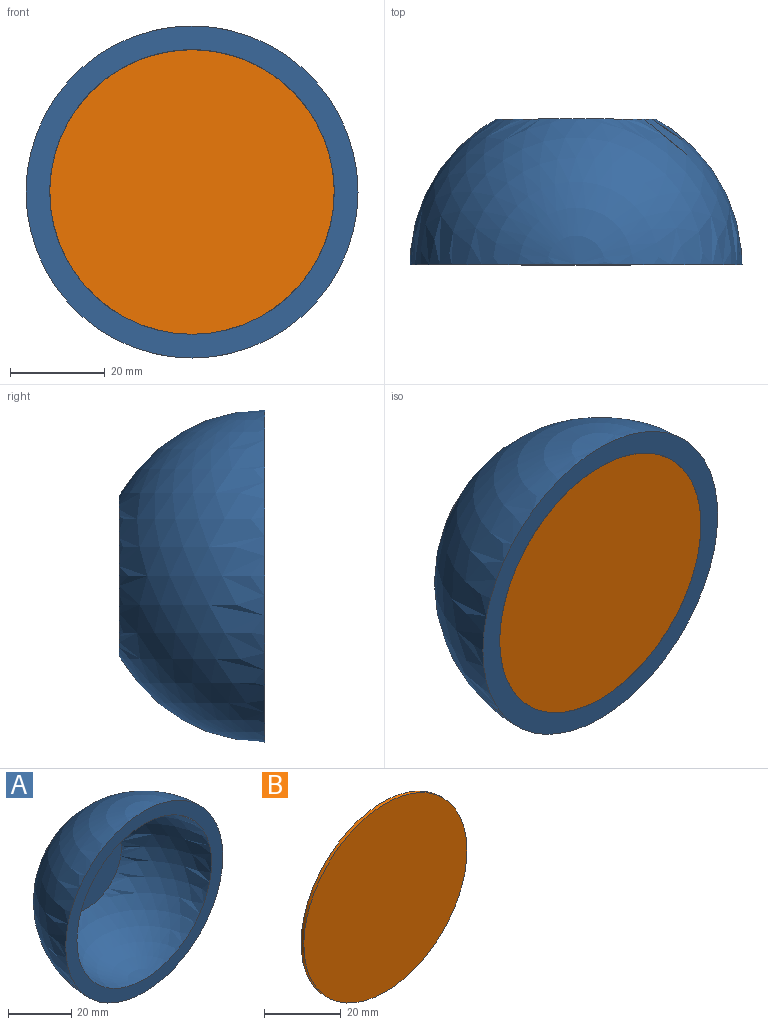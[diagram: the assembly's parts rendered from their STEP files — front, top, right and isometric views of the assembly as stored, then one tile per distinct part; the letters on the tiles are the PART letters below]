
ASSEMBLY  parts=2 mates=1
PART A: 6 faces, bbox 70x35x70 mm
  f0: sphere r=35mm, area 6751.4mm2, adj f1,f2
  f1: plane 70x70mm, normal (0,-1,0), area 1021mm2, adj f0,f3
  f2: plane 33.62x33.62mm, normal (0,1,0), area 809mm2, adj f0,f5
  f3: sphere r=30mm, area 4844.4mm2, adj f1,f4
  f4: plane 30.95x30.95mm, normal (0,-1,0), area 673.9mm2, adj f3,f5
  f5: cylinder r=5mm len=10mm, axis (0,1,0), area 157.1mm2, adj f2,f4
PART B: 3 faces, bbox 60x1x60 mm
  f0: cylinder r=30mm len=60mm, axis (0,1,0), area 188.5mm2, adj f1,f2
  f1: plane 60x60mm, normal (0,-1,0), area 2827.4mm2, adj f0
  f2: plane 60x60mm, normal (0,1,0), area 2827.4mm2, adj f0
PLACE A at identity
PLACE B t=(0,1,0)mm
MATE fastened B.f0 <-> A.f5  axis (0,-1,0) through (0,0,0)mm
